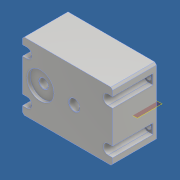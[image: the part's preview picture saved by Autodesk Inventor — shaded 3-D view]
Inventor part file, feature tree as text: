
AUTODESK INVENTOR PART (.ipt)
format: ipt  version: 2018 (Build 220112000, 112)  size: 378,368 bytes
history: native  units: mm
features: extrude x11, projected_geometry x11, sketch x10, chamfer x5, plane x2, mirror x2, fillet x1
ambient origin geometry x8: Origin, YZ Plane, XZ Plane, XY Plane, X Axis, Y Axis, Z Axis, Center Point
bodies: Solid1 (feature_tree)
feature tree (42):
  extrude  "Extrusion1"  Depth=100.0mm
  extrude  "Extrusion3"  Depth=37.5mm
  extrude  "Extrusion4"  Depth=37.5mm
  plane  "Work Plane1"
  plane  "Work Plane2"
  extrude  "Extrusion5"  Depth=10.0mm
  mirror  "Mirror1"
  mirror  "Mirror2"
  extrude  "Extrusion6"  Depth=4.0mm
  extrude  "Extrusion7"  Depth=2.5mm
  extrude  "Extrusion8"  Depth=15.0mm TaperAngle=0.0deg
  extrude  "Extrusion11"  Depth=5.0mm
  extrude  "Extrusion13"  Depth=11.0mm TaperAngle=0.0deg
  extrude  "Extrusion14"  TaperAngle=0.0deg  [1 undecoded]
  chamfer  "Chamfer4"  Distance=22.0mm
  extrude  "Extrusion16"  Depth=12.0mm
  chamfer  "Chamfer5"  [1 undecoded]
  chamfer  "Chamfer6"  [1 undecoded]
  chamfer  "Chamfer7"  Distance=12.0mm
  chamfer  "Chamfer8"  Distance=12.0mm
  fillet  "Fillet1"  Radius=12.0mm
  sketch  "Sketch1"  dims[d0=75.0mm d1=100.0mm]
  sketch  "Sketch2"  dims[d2=37.5mm d3=37.5mm]
  sketch  "Sketch5"  dims[d4=20.0mm d5=37.5mm]
  sketch  "Sketch7"  dims[d6=10.0mm d7=10.2mm]
  sketch  "Sketch8"  dims[d8=10.0mm d9=0.0mm d10=4.0mm]
  projected_geometry  "Projected Loop1"
  projected_geometry  "Projected Loop2"
  projected_geometry  "Projected Loop3"
  projected_geometry  "Projected Loop4"
  projected_geometry  "Projected Loop5"
  projected_geometry  "Projected Loop6"
  projected_geometry  "Projected Loop7"
  projected_geometry  "Projected Loop8"
  sketch  "Sketch9"  dims[d11=4.0mm d12=2.5mm]
  sketch  "Sketch13"  dims[d13=2.5mm d16=15.0mm d17=0.0mm]
  sketch  "Sketch15"  dims[d18=13.75mm d19=5.0mm]
  projected_geometry  "Projected Loop9"
  sketch  "Sketch16"  dims[d20=11.0mm d21=8.0mm d22=0.0mm]
  projected_geometry  "Projected Loop10"
  sketch  "Sketch18"  dims[d23=6.6mm d24=0.0mm d25=0.0mm d26=22.0mm d27=12.0mm d28=0.0mm d29=0.0mm d30=12.0mm d31=12.0mm d32=12.0mm d33=22.0mm d34=22.0mm d35=22.0mm d36=0.0mm d37=0.0mm d38=13.0mm d39=0.0mm d40=6.6mm d41=6.6mm d42=6.6mm d43=6.6mm d44=0.0mm d45=0.0mm d60=12.0mm d61=10.0mm d62=0.0mm d69=20.0mm d70=0.0mm d71=21.0mm d72=0.0mm d73=42.5mm d74=57.5mm d81=0.3mm d82=2.0mm d83=45.0deg d84=30.0mm d85=3.5mm d86=0.0mm d87=0.3mm d88=2.0mm d89=45.0deg d91=0.3mm d92=2.0mm d93=45.0deg d94=0.3mm d95=2.0mm d96=45.0deg d97=2.0mm d98=2.0mm d99=45.0deg d100=10.0mm]
  projected_geometry  "Projected Loop11"
note: 3 required parameter values undecoded (feature->parameter linkage not recoverable at this tier; creation-order binding heuristic only, values carry confidence <= 0.55)
